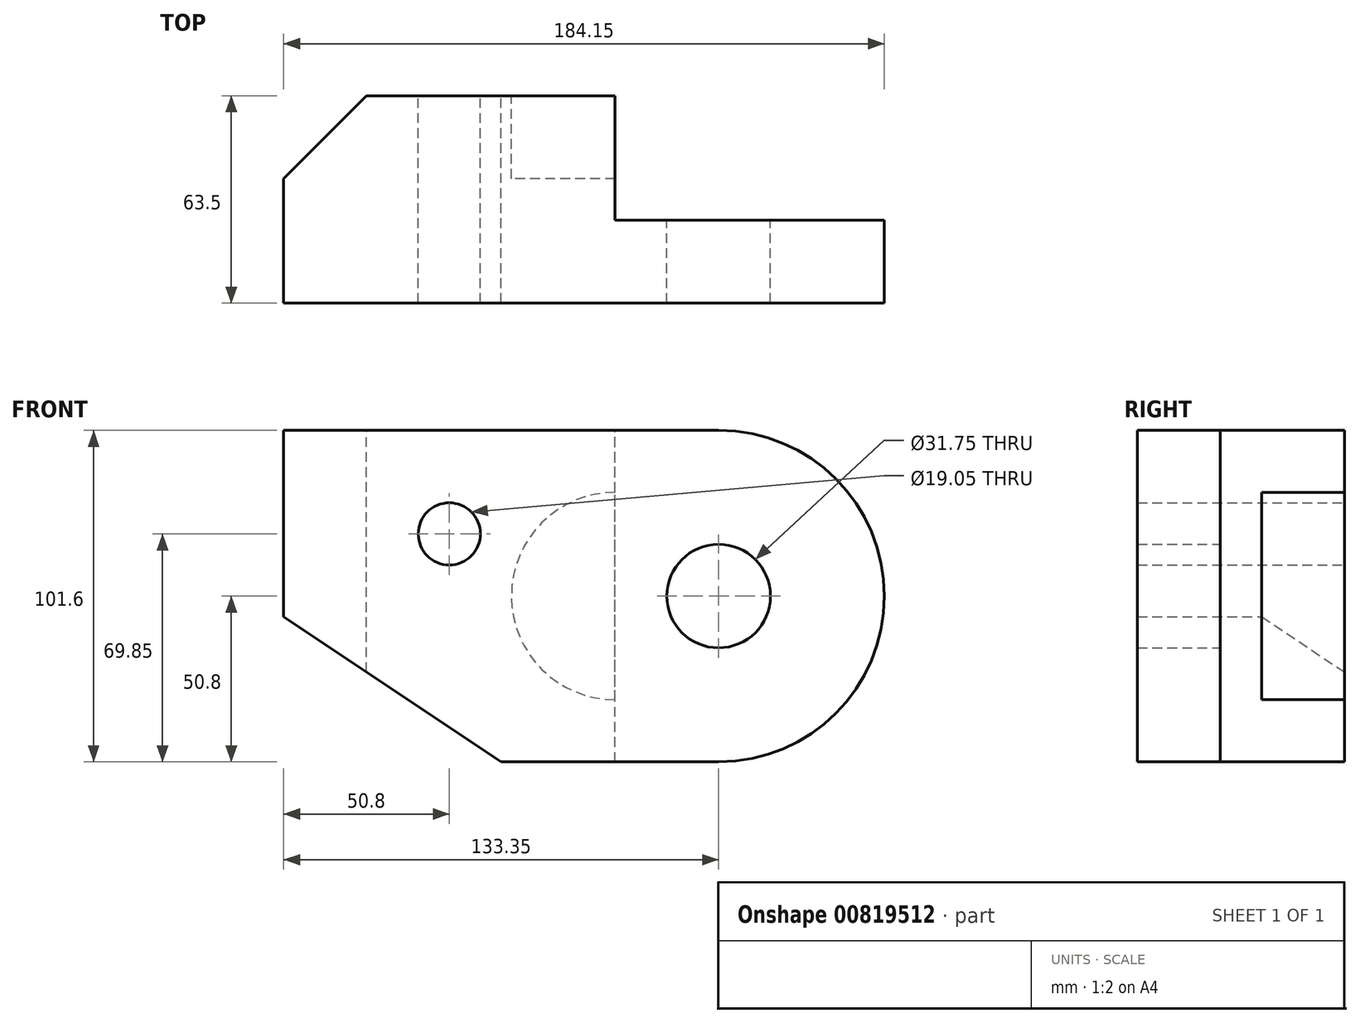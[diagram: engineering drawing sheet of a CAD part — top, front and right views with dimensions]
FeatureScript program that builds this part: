
annotation { "Feature Type Name" : "Feature", "Feature Type Description" : "" }
export const myFeature = defineFeature(function(context is Context, id is Id, definition is map)
    precondition{}
    {
        {
            var Q0;
            Q0=qCreatedBy(makeId("Front.planeOp"),FACE);
            var sketch = newSketch(context, id + "F0", { "sketchPlane" : qUnion([Q0])});
            skCircle(sketch, "E0", {"center": v(0, 0) * mm, "radius": 15.88 * mm});
            skArc(sketch, "E1", {"start": v(0, -50.8) * mm, "mid": v(50.8, 0) * mm, "end": v(0, 50.8) * mm});
            skLineSegment(sketch, "E2", {"start": v(0, 50.8) * mm, "end": v(-133.35, 50.8) * mm});
            skLineSegment(sketch, "E3", {"start": v(0, -50.8) * mm, "end": v(-66.68, -50.8) * mm});
            skLineSegment(sketch, "E4", {"start": v(-133.35, -6.35) * mm, "end": v(-133.35, 50.8) * mm});
            skCircle(sketch, "E5", {"center": v(-82.55, 19.05) * mm, "radius": 9.53 * mm});
            skLineSegment(sketch, "E6", {"start": v(-133.35, -6.35) * mm, "end": v(-66.68, -50.8) * mm});
            skSolve(sketch);
        }
        {
            var Q0;
            Q0=makeQuery(id+"F0.imprint","IMPRINT",FACE,{"disambiguationData":[TD([[makeQuery(id+"F0.imprint","IMPRINT",EDGE,{"derivedFrom":sQuery(id+"F0.wireOp",EDGE,"E0")}),-1.0]])]});
            extrude(context, id + "F1", {"entities" : qUnion([Q0]), "endBound" : BoundingType.SYMMETRIC, "depth" : 63.5 * mm, "offsetDistance" : 25.4 * mm});
        }
        {
            var Q0;
            Q0=makeQuery(id+"F1.opExtrude","SWEPT_FACE",FACE,{"disambiguationData":[OSD([sQuery(id+"F0.wireOp",EDGE,"E2")])]});
            var sketch = newSketch(context, id + "F2", { "sketchPlane" : qUnion([Q0])});
            skLineSegment(sketch, "E7", {"start": v(50.8, -6.35) * mm, "end": v(-31.75, -6.35) * mm});
            skLineSegment(sketch, "E8", {"start": v(-31.75, -6.35) * mm, "end": v(-31.75, 31.75) * mm});
            skLineSegment(sketch, "E9", {"start": v(50.8, 31.75) * mm, "end": v(-31.75, 31.75) * mm});
            skLineSegment(sketch, "E10", {"start": v(50.8, 31.75) * mm, "end": v(50.8, -6.35) * mm});
            skLineSegment(sketch, "E11", {"start": v(-107.95, -31.75) * mm, "end": v(-107.95, 31.75) * mm});
            skLineSegment(sketch, "E12", {"start": v(-133.35, 31.75) * mm, "end": v(-133.35, 6.35) * mm});
            skLineSegment(sketch, "E13", {"start": v(-133.35, 6.35) * mm, "end": v(-107.95, 31.75) * mm});
            skLineSegment(sketch, "E14", {"start": v(-133.35, 31.75) * mm, "end": v(-107.95, 31.75) * mm});
            skPoint(sketch, "E15.start.orphan", {"position": v(-31.75, -31.75) * mm});
            skSolve(sketch);
        }
        {
            var Q0;
            Q0=makeQuery(id+"F2.imprint","IMPRINT",FACE,{"disambiguationData":[TD([[makeQuery(id+"F2.imprint","IMPRINT",EDGE,{"derivedFrom":sQuery(id+"F2.wireOp",EDGE,"E12")}),-1.0]])]});
            var Q1;
            {var subQ0=sQuery(id+"F2.wireOp",EDGE,"E10");Q1=makeQuery(id+"F2.imprint","IMPRINT",FACE,{"disambiguationData":[TD([[makeQuery(id+"F2.imprint","IMPRINT",EDGE,{"derivedFrom":subQ0}),-1.0]])]});}
            var Q2;
            {var subQ0=sQuery(id+"F2.wireOp",EDGE,"E8");Q2=makeQuery(id+"F2.imprint","IMPRINT",FACE,{"disambiguationData":[TD([[makeQuery(id+"F2.imprint","IMPRINT",EDGE,{"derivedFrom":subQ0}),-1.0]])]});}
            extrude(context, id + "F3", {"entities" : qUnion([Q0, Q1, Q2]), "operationType" : NewBodyOperationType.REMOVE, "oppositeDirection" : true, "depth" : 127 * mm, "offsetDistance" : 25.4 * mm});
        }
        {
            var Q0;
            Q0=makeQuery(id+"F1.opExtrude","CAP_FACE",FACE,{"disambiguationData":[OSD([sQuery(id+"F0.wireOp",EDGE,"E0"),sQuery(id+"F0.wireOp",EDGE,"E1"),sQuery(id+"F0.wireOp",EDGE,"E2"),sQuery(id+"F0.wireOp",EDGE,"E4"),sQuery(id+"F0.wireOp",EDGE,"E5"),sQuery(id+"F0.wireOp",EDGE,"E3"),sQuery(id+"F0.wireOp",EDGE,"E6")])],"isStart":true});
            var sketch = newSketch(context, id + "F4", { "sketchPlane" : qUnion([Q0])});
            skArc(sketch, "E16", {"start": v(31.75, -31.75) * mm, "mid": v(63.5, 0) * mm, "end": v(31.75, 31.75) * mm});
            skLineSegment(sketch, "E17", {"start": v(31.75, 0) * mm, "end": v(31.75, 31.75) * mm});
            skLineSegment(sketch, "E18", {"start": v(31.75, 0) * mm, "end": v(31.75, -31.75) * mm});
            skSolve(sketch);
        }
        {
            var Q0;
            Q0=makeQuery(id+"F4.imprint","IMPRINT",FACE,{"disambiguationData":[TD([[makeQuery(id+"F4.imprint","IMPRINT",EDGE,{"derivedFrom":sQuery(id+"F4.wireOp",EDGE,"E16")}),1.0]])]});
            extrude(context, id + "F5", {"entities" : qUnion([Q0]), "operationType" : NewBodyOperationType.REMOVE, "oppositeDirection" : true, "depth" : 25.4 * mm, "offsetDistance" : 25.4 * mm});
        }
    });
